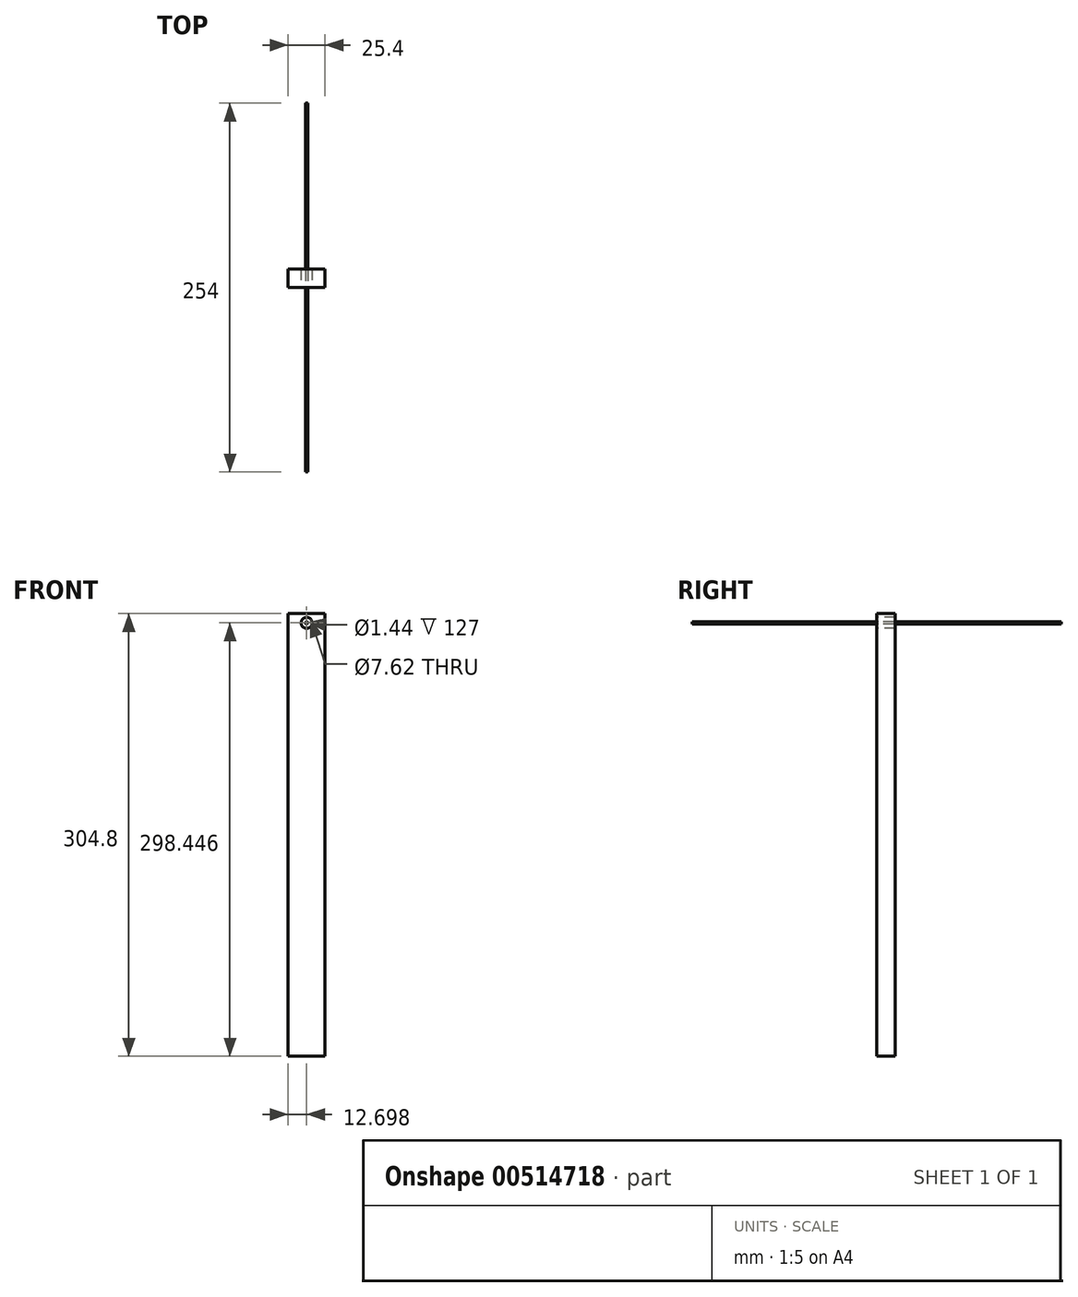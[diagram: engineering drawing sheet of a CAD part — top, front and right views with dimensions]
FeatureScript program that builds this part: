
annotation { "Feature Type Name" : "Feature", "Feature Type Description" : "" }
export const myFeature = defineFeature(function(context is Context, id is Id, definition is map)
    precondition{}
    {
        {
            var Q0;
            Q0=qCreatedBy(makeId("Front.planeOp"),FACE);
            var sketch = newSketch(context, id + "F0", { "sketchPlane" : qUnion([Q0])});
            skLineSegment(sketch, "E0.bottom", {"start": v(-22.57, 218.87) * mm, "end": v(-47.97, 218.87) * mm});
            skLineSegment(sketch, "E0.top", {"start": v(-22.57, -85.93) * mm, "end": v(-47.97, -85.93) * mm});
            skLineSegment(sketch, "E0.left", {"start": v(-22.57, 218.87) * mm, "end": v(-22.57, -85.93) * mm});
            skLineSegment(sketch, "E0.right", {"start": v(-47.97, 218.87) * mm, "end": v(-47.97, -85.93) * mm});
            skPoint(sketch, "E0.middle", {"position": v(-35.27, 66.47) * mm});
            skSolve(sketch);
        }
        {
            var Q0;
            Q0=makeQuery(id+"F0.imprint","IMPRINT",FACE,{"disambiguationData":[TD([[makeQuery(id+"F0.imprint","IMPRINT",EDGE,{"derivedFrom":sQuery(id+"F0.wireOp",EDGE,"E0.bottom")}),1.0]])]});
            extrude(context, id + "F1", {"entities" : qUnion([Q0]), "depth" : 12.7 * mm, "offsetDistance" : 25.4 * mm});
        }
        {
            var Q0;
            Q0=makeQuery(id+"F1.opExtrude","CAP_FACE",FACE,{"disambiguationData":[OSD([sQuery(id+"F0.wireOp",EDGE,"E0.bottom"),sQuery(id+"F0.wireOp",EDGE,"E0.top"),sQuery(id+"F0.wireOp",EDGE,"E0.left"),sQuery(id+"F0.wireOp",EDGE,"E0.right")])],"isStart":false});
            var sketch = newSketch(context, id + "F2", { "sketchPlane" : qUnion([Q0])});
            skCircle(sketch, "E1", {"center": v(-35.27, 212.52) * mm, "radius": 3.81 * mm});
            skSolve(sketch);
        }
        {
            var Q0;
            Q0 = qSketchRegion(id + "F2", true);
            extrude(context, id + "F3", {"entities" : qUnion([Q0]), "operationType" : NewBodyOperationType.REMOVE, "oppositeDirection" : true, "depth" : 25.4 * mm, "offsetDistance" : 25.4 * mm});
        }
        {
            var Q0;
            Q0=makeQuery(id+"F1.opExtrude","CAP_FACE",FACE,{"disambiguationData":[OSD([sQuery(id+"F0.wireOp",EDGE,"E0.bottom"),sQuery(id+"F0.wireOp",EDGE,"E0.top"),sQuery(id+"F0.wireOp",EDGE,"E0.left"),sQuery(id+"F0.wireOp",EDGE,"E0.right")])],"isStart":false});
            var sketch = newSketch(context, id + "F4", { "sketchPlane" : qUnion([Q0])});
            skCircle(sketch, "E2", {"center": v(-35.27, 212.52) * mm, "radius": 0.72 * mm});
            skSolve(sketch);
        }
        {
            var Q0;
            Q0=makeQuery(id+"F4.imprint","IMPRINT",FACE,{"disambiguationData":[TD([[makeQuery(id+"F4.imprint","IMPRINT",EDGE,{"derivedFrom":sQuery(id+"F4.wireOp",EDGE,"E2")}),1.0]])]});
            extrude(context, id + "F5", {"entities" : qUnion([Q0]), "depth" : 127 * mm, "offsetDistance" : 25.4 * mm});
        }
        {
            var Q0;
            Q0=makeQuery(id+"F5.opExtrude","CAP_FACE",FACE,{"disambiguationData":[OSD([sQuery(id+"F4.wireOp",EDGE,"E2")])],"isStart":true});
            var sketch = newSketch(context, id + "F6", { "sketchPlane" : qUnion([Q0])});
            skCircle(sketch, "E3", {"center": v(35.27, 212.52) * mm, "radius": 0.74 * mm});
            skSolve(sketch);
        }
        {
            var Q0;
            Q0=makeQuery(id+"F6.imprint","IMPRINT",FACE,{"disambiguationData":[TD([[makeQuery(id+"F6.imprint","IMPRINT",EDGE,{"derivedFrom":sQuery(id+"F6.wireOp",EDGE,"E3")}),1.0]])]});
            extrude(context, id + "F7", {"entities" : qUnion([Q0]), "operationType" : NewBodyOperationType.ADD, "depth" : 127 * mm, "offsetDistance" : 25.4 * mm});
        }
    });
